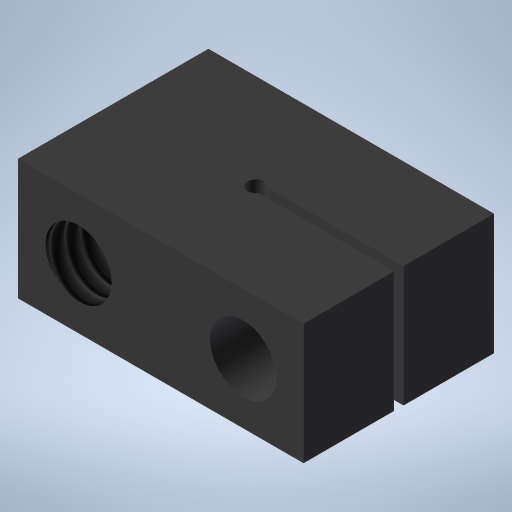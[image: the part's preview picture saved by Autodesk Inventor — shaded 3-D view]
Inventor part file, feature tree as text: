
AUTODESK INVENTOR PART (.ipt)
format: ipt  version: 2024 (Build 280153000, 153)  size: 226,304 bytes
history: native  units: in
note: dims shown in document units (in); Inventor stores cm internally (conversion verified against a paired STEP export)
features: sketch x3, extrude x2, hole x2, thread x2
ambient origin geometry x8: Origin, YZ Plane, XZ Plane, XY Plane, X Axis, Y Axis, Z Axis, Center Point
bodies: Solid1 (feature_tree)
feature tree (9):
  extrude  "Extrusion1"  Depth=0.3937in
  sketch  "Sketch2"  dims[d2=0.2953in d3=0.036in]
  hole  "Hole1"  [1 undecoded]
  hole  "Hole2"  [1 undecoded]
  thread  "Thread1"  [1 undecoded]
  thread  "Thread2"  [1 undecoded]
  extrude  "Extrusion2"  Depth=0.3937in
  sketch  "Sketch1"  dims[d0=0.5906in d1=0.3937in]
  sketch  "Sketch3"  dims[d4=0.01in d5=0.01in d6=0.25in d7=0.0in d8=135.0deg d9=0.138in d10=45.0deg d11=0.138in d12=0.138in d13=0.75in d14=0.375in d15=0.25in d16=0.5635in d17=1.0in d18=0.8108in d19=0.138in d20=0.75in d21=0.375in d22=0.25in d23=0.5635in d24=1.0in d25=0.8108in d26=0.3937in d27=0.0in d28=0.1809in d29=0.0in d30=0.04in d31=0.1378in d32=0.0in]
note: 4 required parameter values undecoded (feature->parameter linkage not recoverable at this tier; creation-order binding heuristic only, values carry confidence <= 0.55)
